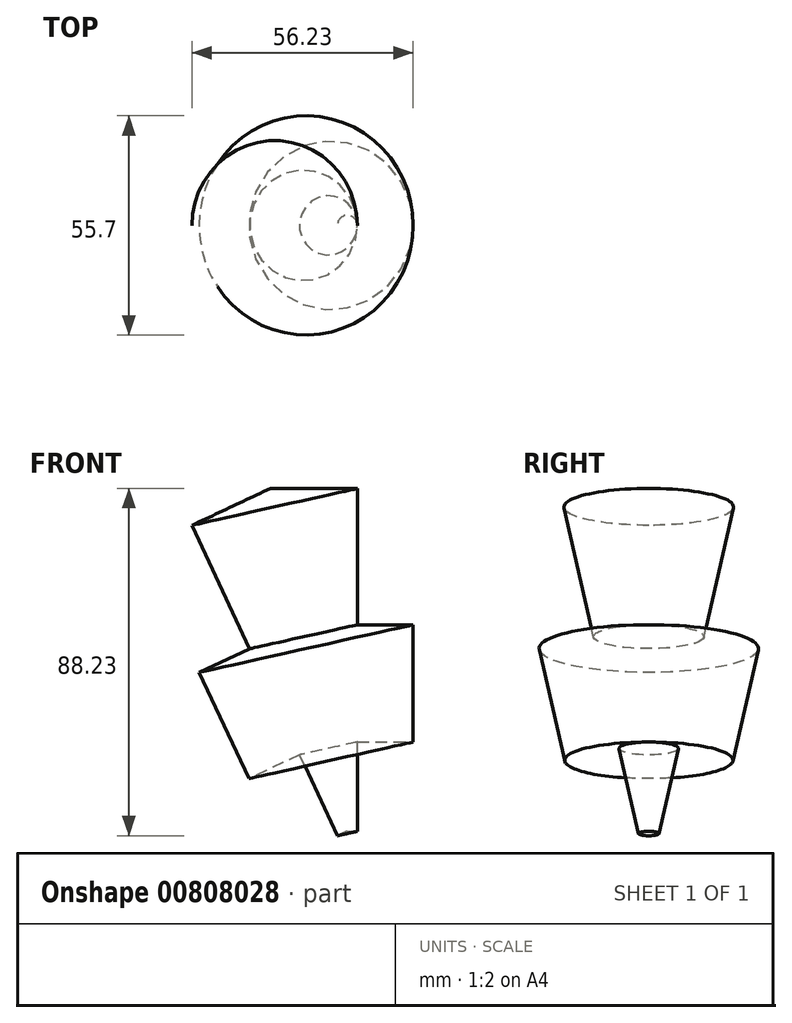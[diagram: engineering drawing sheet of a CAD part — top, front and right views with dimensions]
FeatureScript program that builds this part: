
annotation { "Feature Type Name" : "Feature", "Feature Type Description" : "" }
export const myFeature = defineFeature(function(context is Context, id is Id, definition is map)
    precondition{}
    {
        {
            var Q0;
            Q0=qCreatedBy(makeId("Front.planeOp"),FACE);
            var sketch = newSketch(context, id + "F0", { "sketchPlane" : qUnion([Q0])});
            skLineSegment(sketch, "E0.bottom", {"start": v(-39.58, 46.39) * mm, "end": v(34.47, 46.39) * mm});
            skLineSegment(sketch, "E0.top", {"start": v(-39.58, -40.71) * mm, "end": v(34.47, -40.71) * mm});
            skLineSegment(sketch, "E0.left", {"start": v(-39.58, 46.39) * mm, "end": v(-39.58, -40.71) * mm});
            skLineSegment(sketch, "E0.right", {"start": v(34.47, 46.39) * mm, "end": v(34.47, -40.71) * mm});
            skLineSegment(sketch, "E1.bottom", {"start": v(34.47, 11.77) * mm, "end": v(48.66, 11.77) * mm});
            skLineSegment(sketch, "E1.top", {"start": v(34.47, -18.02) * mm, "end": v(48.66, -18.02) * mm});
            skLineSegment(sketch, "E1.left", {"start": v(34.47, 11.77) * mm, "end": v(34.47, -18.02) * mm});
            skLineSegment(sketch, "E1.right", {"start": v(48.66, 11.77) * mm, "end": v(48.66, -18.02) * mm});
            skLineSegment(sketch, "E2", {"start": v(11.2, 51.78) * mm, "end": v(33.9, -50.08) * mm});
            skSolve(sketch);
        }
        {
            var Q0;
            {var subQ0=sQuery(id+"F0.wireOp",EDGE,"E0.right");var subQ1=sQuery(id+"F0.wireOp",EDGE,"E0.bottom");var subQ2=makeQuery(id+"F0.imprint","INTERSECT",VERTEX,{"derivedFrom":[subQ1,subQ0]});Q0=makeQuery(id+"F0.imprint","IMPRINT",FACE,{"disambiguationData":[TD([[makeQuery(id+"F0.imprint","IMPRINT",EDGE,{"disambiguationData":[TD([[subQ2,1.0]])],"derivedFrom":subQ1}),-1.0]])]});}
            var Q1;
            {var subQ0=sQuery(id+"F0.wireOp",EDGE,"E1.bottom");Q1=makeQuery(id+"F0.imprint","IMPRINT",FACE,{"disambiguationData":[TD([[makeQuery(id+"F0.imprint","IMPRINT",EDGE,{"derivedFrom":subQ0}),-1.0]])]});}
            var Q2;
            Q2=sQuery(id+"F0.wireOp",EDGE,"E2");
            revolve(context, id + "F1", {"surfaceOperationType" : NewSurfaceOperationType.NEW, "entities" : qUnion([Q0, Q1]), "axis" : qUnion([Q2]), "revolveType" : RevolveType.FULL});
        }
    });
